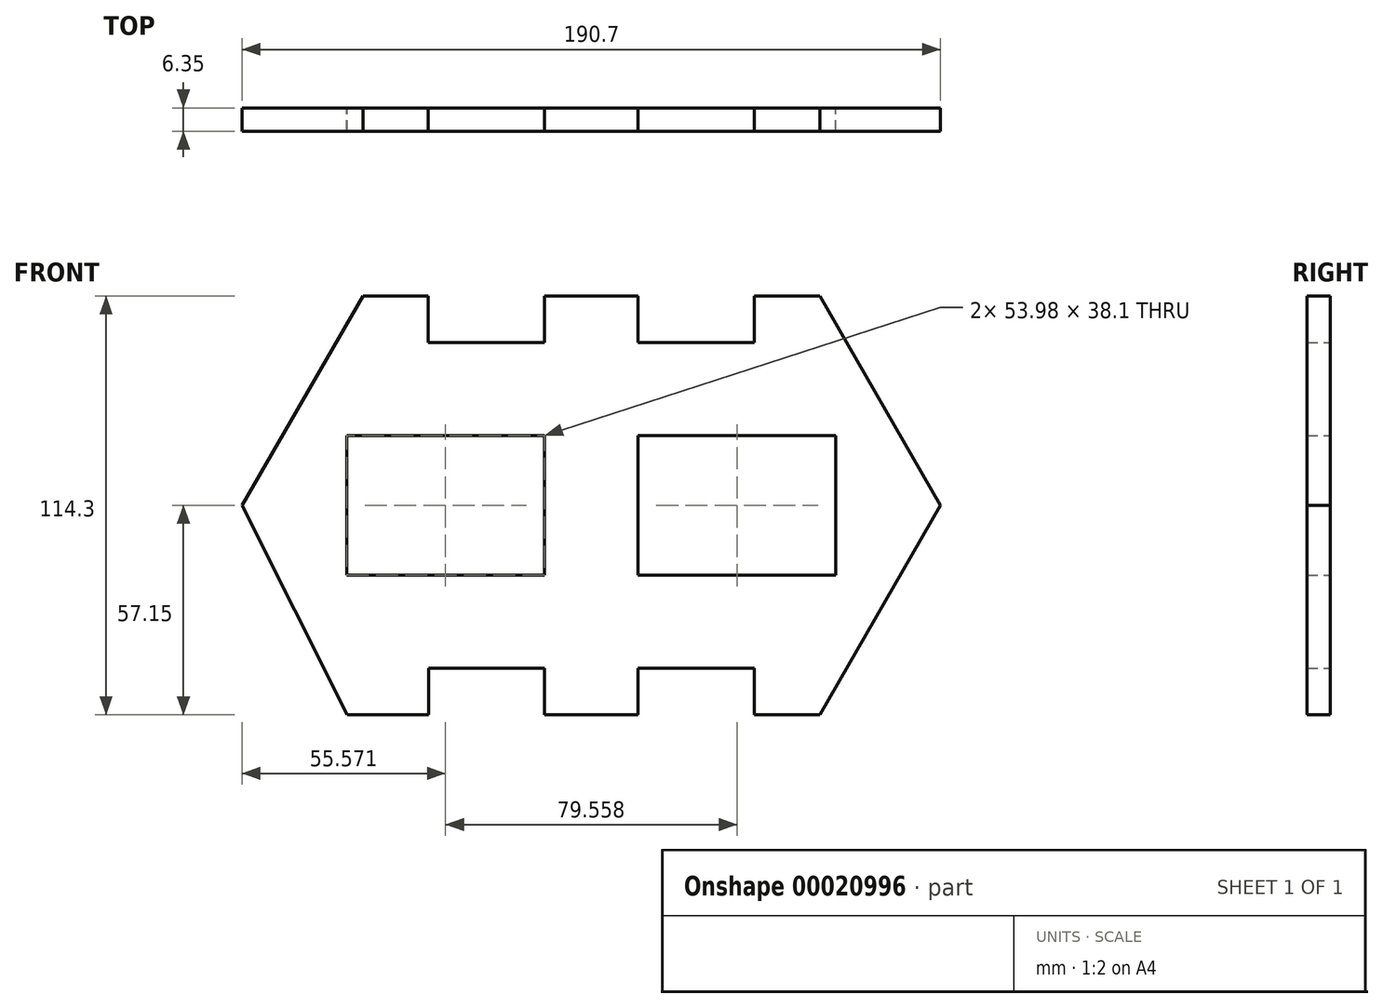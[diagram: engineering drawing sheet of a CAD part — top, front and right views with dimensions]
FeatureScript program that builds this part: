
annotation { "Feature Type Name" : "Feature", "Feature Type Description" : "" }
export const myFeature = defineFeature(function(context is Context, id is Id, definition is map)
    precondition{}
    {
        {
            var Q0;
            Q0=qCreatedBy(makeId("Front.planeOp"),FACE);
            var sketch = newSketch(context, id + "F0", { "sketchPlane" : qUnion([Q0])});
            skLineSegment(sketch, "E0.rect.bottom", {"start": v(-62.35, 57.15) * mm, "end": v(-44.54, 57.15) * mm});
            skLineSegment(sketch, "E0.rect.top", {"start": v(-66.68, -57.15) * mm, "end": v(-44.45, -57.15) * mm});
            skPoint(sketch, "E0.rect.middle", {"position": v(0, 0) * mm});
            skLineSegment(sketch, "E1.rect.bottom", {"start": v(-12.8, 57.15) * mm, "end": v(-12.8, 57.15) * mm});
            skLineSegment(sketch, "E1.rect.top", {"start": v(-12.8, -57.15) * mm, "end": v(12.8, -57.15) * mm});
            skLineSegment(sketch, "E1.rect.left", {"start": v(-12.8, 57.15) * mm, "end": v(-12.8, 44.45) * mm});
            skLineSegment(sketch, "E1.rect.right", {"start": v(12.8, 57.15) * mm, "end": v(12.8, 57.15) * mm});
            skLineSegment(sketch, "E2", {"start": v(-12.8, 57.15) * mm, "end": v(12.8, 57.15) * mm});
            skLineSegment(sketch, "E3", {"start": v(12.8, 57.15) * mm, "end": v(12.8, 44.45) * mm});
            skLineSegment(sketch, "E4.top", {"start": v(-12.8, 44.45) * mm, "end": v(-44.54, 44.45) * mm});
            skLineSegment(sketch, "E4.right", {"start": v(-44.54, 57.15) * mm, "end": v(-44.54, 44.45) * mm});
            skLineSegment(sketch, "E5.top", {"start": v(12.8, 44.45) * mm, "end": v(44.54, 44.45) * mm});
            skLineSegment(sketch, "E5.right", {"start": v(44.54, 57.15) * mm, "end": v(44.54, 44.45) * mm});
            skLineSegment(sketch, "E6.rect.bottom", {"start": v(-66.77, 19.05) * mm, "end": v(-12.8, 19.05) * mm});
            skLineSegment(sketch, "E6.rect.top", {"start": v(-66.77, -19.05) * mm, "end": v(-12.8, -19.05) * mm});
            skLineSegment(sketch, "E6.rect.left", {"start": v(-66.77, 19.05) * mm, "end": v(-66.77, -19.05) * mm});
            skLineSegment(sketch, "E6.rect.right", {"start": v(66.77, 19.05) * mm, "end": v(66.77, -19.05) * mm});
            skLineSegment(sketch, "E7.MirrorCS", {"start": v(-44.45, -57.15) * mm, "end": v(-44.45, -44.45) * mm});
            skLineSegment(sketch, "E8.MirrorCS", {"start": v(12.8, -44.45) * mm, "end": v(44.54, -44.45) * mm});
            skLineSegment(sketch, "E9.MirrorCS", {"start": v(44.45, -57.15) * mm, "end": v(44.45, -44.45) * mm});
            skLineSegment(sketch, "E10", {"start": v(-62.35, 57.15) * mm, "end": v(-95.35, 0) * mm});
            skLineSegment(sketch, "E11.MirrorCS", {"start": v(-66.68, -57.15) * mm, "end": v(-95.35, 0) * mm});
            skPoint(sketch, "E12.start.orphan", {"position": v(0, 57.15) * mm});
            skLineSegment(sketch, "E13.trimOffspring", {"start": v(12.8, 19.05) * mm, "end": v(12.8, -19.05) * mm});
            skLineSegment(sketch, "E14.trimOffspring", {"start": v(-12.8, 19.05) * mm, "end": v(-12.8, -19.05) * mm});
            skPoint(sketch, "E15.orphan", {"position": v(95.35, 57.15) * mm});
            skPoint(sketch, "E16.orphan", {"position": v(95.35, -57.15) * mm});
            skLineSegment(sketch, "E17.trimOffspring", {"start": v(44.45, -57.15) * mm, "end": v(62.35, -57.15) * mm});
            skLineSegment(sketch, "E18.trimOffspring", {"start": v(44.54, 57.15) * mm, "end": v(62.35, 57.15) * mm});
            skPoint(sketch, "E19.orphan", {"position": v(-95.35, 57.15) * mm});
            skPoint(sketch, "E20.orphan", {"position": v(-95.35, -57.15) * mm});
            skLineSegment(sketch, "E21.trimOffspring", {"start": v(12.8, 19.05) * mm, "end": v(66.77, 19.05) * mm});
            skLineSegment(sketch, "E22.trimOffspring", {"start": v(12.8, -19.05) * mm, "end": v(66.77, -19.05) * mm});
            skPoint(sketch, "E23.trimOffspring.end.orphan", {"position": v(0, -57.15) * mm});
            skPoint(sketch, "E24.trimOffspring.end.orphan", {"position": v(95.35, 0) * mm});
            skLineSegment(sketch, "E25.trimOffspring", {"start": v(-12.8, -44.45) * mm, "end": v(-12.8, -57.15) * mm});
            skLineSegment(sketch, "E26.trimOffspring", {"start": v(12.8, -44.45) * mm, "end": v(12.8, -57.15) * mm});
            skLineSegment(sketch, "E27", {"start": v(62.35, 57.15) * mm, "end": v(95.35, 0) * mm});
            skLineSegment(sketch, "E28", {"start": v(95.35, 0) * mm, "end": v(62.35, -57.15) * mm});
            skLineSegment(sketch, "E29", {"start": v(-44.45, -44.45) * mm, "end": v(-12.8, -44.45) * mm});
            skSolve(sketch);
        }
        {
            var Q0;
            Q0=makeQuery(id+"F0.imprint","IMPRINT",FACE,{"disambiguationData":[TD([[makeQuery(id+"F0.imprint","IMPRINT",EDGE,{"derivedFrom":sQuery(id+"F0.wireOp",EDGE,"E0.rect.bottom")}),-1.0]])]});
            extrude(context, id + "F1", {"entities" : qUnion([Q0]), "depth" : 6.35 * mm});
        }
    });
